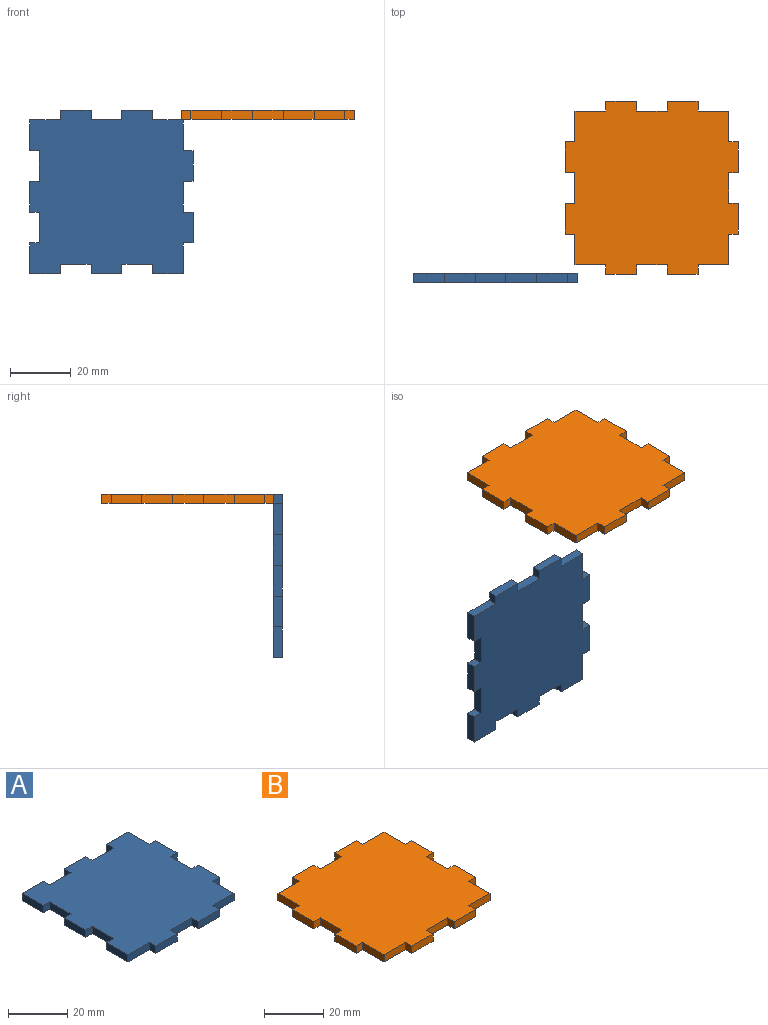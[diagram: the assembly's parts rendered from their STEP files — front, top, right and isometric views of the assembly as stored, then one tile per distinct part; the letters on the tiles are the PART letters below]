
ASSEMBLY  parts=2 mates=1
PART A: 38 faces, bbox 54x54x3 mm
  f0: plane 10.16x3mm, normal (0,1,0), area 30.5mm2, adj f1,f35,f36,f37
  f1: plane 3.18x3mm, normal (-1,0,0), area 9.5mm2, adj f0,f2,f36,f37
  f2: plane 10.16x3mm, normal (0,1,0), area 30.5mm2, adj f1,f3,f36,f37
  f3: plane 3.18x3mm, normal (1,0,0), area 9.5mm2, adj f2,f4,f36,f37
  f4: plane 10.16x3mm, normal (0,1,0), area 30.5mm2, adj f3,f5,f36,f37
  f5: plane 3.18x3mm, normal (-1,0,0), area 9.5mm2, adj f4,f6,f36,f37
  f6: plane 10.16x3mm, normal (0,1,0), area 30.5mm2, adj f5,f7,f36,f37
  f7: plane 3.18x3mm, normal (1,0,0), area 9.5mm2, adj f6,f8,f36,f37
  f8: plane 10.16x3mm, normal (0,1,0), area 30.5mm2, adj f7,f9,f36,f37
  f9: plane 10.16x3mm, normal (-1,0,0), area 30.5mm2, adj f8,f10,f36,f37
  f10: plane 3.18x3mm, normal (0,-1,0), area 9.5mm2, adj f9,f11,f36,f37
  f11: plane 10.16x3mm, normal (-1,0,0), area 30.5mm2, adj f10,f12,f36,f37
  f12: plane 3.18x3mm, normal (0,1,0), area 9.5mm2, adj f11,f13,f36,f37
  f13: plane 10.16x3mm, normal (-1,0,0), area 30.5mm2, adj f12,f14,f36,f37
  f14: plane 3.18x3mm, normal (0,-1,0), area 9.5mm2, adj f13,f15,f36,f37
  f15: plane 10.16x3mm, normal (-1,0,0), area 30.5mm2, adj f14,f16,f36,f37
  f16: plane 3.18x3mm, normal (0,1,0), area 9.5mm2, adj f15,f17,f36,f37
  f17: plane 10.16x3mm, normal (-1,0,0), area 30.5mm2, adj f16,f18,f36,f37
  f18: plane 10.16x3mm, normal (0,-1,0), area 30.5mm2, adj f17,f19,f36,f37
  f19: plane 3.18x3mm, normal (-1,0,0), area 9.5mm2, adj f18,f20,f36,f37
  f20: plane 10.16x3mm, normal (0,-1,0), area 30.5mm2, adj f19,f21,f36,f37
  f21: plane 3.18x3mm, normal (1,0,0), area 9.5mm2, adj f20,f22,f36,f37
  f22: plane 10.16x3mm, normal (0,-1,0), area 30.5mm2, adj f21,f23,f36,f37
  f23: plane 3.18x3mm, normal (-1,0,0), area 9.5mm2, adj f22,f24,f36,f37
  f24: plane 10.16x3mm, normal (0,-1,0), area 30.5mm2, adj f23,f25,f36,f37
  f25: plane 3.18x3mm, normal (1,0,0), area 9.5mm2, adj f24,f26,f36,f37
  f26: plane 10.16x3mm, normal (0,-1,0), area 30.5mm2, adj f25,f27,f36,f37
  f27: plane 10.16x3mm, normal (1,0,0), area 30.5mm2, adj f26,f28,f36,f37
  f28: plane 3.18x3mm, normal (0,-1,0), area 9.5mm2, adj f27,f29,f36,f37
  f29: plane 10.16x3mm, normal (1,0,0), area 30.5mm2, adj f28,f30,f36,f37
  f30: plane 3.18x3mm, normal (0,1,0), area 9.5mm2, adj f29,f31,f36,f37
  f31: plane 10.16x3mm, normal (1,0,0), area 30.5mm2, adj f30,f32,f36,f37
  f32: plane 3.18x3mm, normal (0,-1,0), area 9.5mm2, adj f31,f33,f36,f37
  f33: plane 10.16x3mm, normal (1,0,0), area 30.5mm2, adj f32,f34,f36,f37
  f34: plane 3.18x3mm, normal (0,1,0), area 9.5mm2, adj f33,f35,f36,f37
  f35: plane 10.16x3mm, normal (1,0,0), area 30.5mm2, adj f0,f34,f36,f37
  f36: plane 53.98x53.98mm, normal (0,0,1), area 2580.6mm2, adj f0,f1,f2,f3,f4,f5,f6,f7
  f37: plane 53.98x53.98mm, normal (0,0,-1), area 2580.6mm2, adj f0,f1,f2,f3,f4,f5,f6,f7
PART B: 38 faces, bbox 57.2x57.2x3 mm
  f0: plane 10.16x3mm, normal (-1,0,0), area 30.5mm2, adj f1,f35,f36,f37
  f1: plane 10.16x3mm, normal (0,-1,0), area 30.5mm2, adj f0,f2,f36,f37
  f2: plane 3.18x3mm, normal (-1,0,0), area 9.5mm2, adj f1,f3,f36,f37
  f3: plane 10.16x3mm, normal (0,-1,0), area 30.5mm2, adj f2,f4,f36,f37
  f4: plane 3.18x3mm, normal (1,0,0), area 9.5mm2, adj f3,f5,f36,f37
  f5: plane 10.16x3mm, normal (0,-1,0), area 30.5mm2, adj f4,f6,f36,f37
  f6: plane 3.18x3mm, normal (-1,0,0), area 9.5mm2, adj f5,f7,f36,f37
  f7: plane 10.16x3mm, normal (0,-1,0), area 30.5mm2, adj f6,f8,f36,f37
  f8: plane 3.18x3mm, normal (1,0,0), area 9.5mm2, adj f7,f9,f36,f37
  f9: plane 10.16x3mm, normal (0,-1,0), area 30.5mm2, adj f8,f10,f36,f37
  f10: plane 10.16x3mm, normal (1,0,0), area 30.5mm2, adj f9,f11,f36,f37
  f11: plane 3.18x3mm, normal (0,-1,0), area 9.5mm2, adj f10,f12,f36,f37
  f12: plane 10.16x3mm, normal (1,0,0), area 30.5mm2, adj f11,f13,f36,f37
  f13: plane 3.18x3mm, normal (0,1,0), area 9.5mm2, adj f12,f14,f36,f37
  f14: plane 10.16x3mm, normal (1,0,0), area 30.5mm2, adj f13,f15,f36,f37
  f15: plane 3.18x3mm, normal (0,-1,0), area 9.5mm2, adj f14,f16,f36,f37
  f16: plane 10.16x3mm, normal (1,0,0), area 30.5mm2, adj f15,f17,f36,f37
  f17: plane 3.18x3mm, normal (0,1,0), area 9.5mm2, adj f16,f18,f36,f37
  f18: plane 10.16x3mm, normal (1,0,0), area 30.5mm2, adj f17,f19,f36,f37
  f19: plane 10.16x3mm, normal (0,1,0), area 30.5mm2, adj f18,f20,f36,f37
  f20: plane 3.18x3mm, normal (1,0,0), area 9.5mm2, adj f19,f21,f36,f37
  f21: plane 10.16x3mm, normal (0,1,0), area 30.5mm2, adj f20,f22,f36,f37
  f22: plane 3.18x3mm, normal (-1,0,0), area 9.5mm2, adj f21,f23,f36,f37
  f23: plane 10.16x3mm, normal (0,1,0), area 30.5mm2, adj f22,f24,f36,f37
  f24: plane 3.18x3mm, normal (1,0,0), area 9.5mm2, adj f23,f25,f36,f37
  f25: plane 10.16x3mm, normal (0,1,0), area 30.5mm2, adj f24,f26,f36,f37
  f26: plane 3.18x3mm, normal (-1,0,0), area 9.5mm2, adj f25,f27,f36,f37
  f27: plane 10.16x3mm, normal (0,1,0), area 30.5mm2, adj f26,f28,f36,f37
  f28: plane 10.16x3mm, normal (-1,0,0), area 30.5mm2, adj f27,f29,f36,f37
  f29: plane 3.18x3mm, normal (0,1,0), area 9.5mm2, adj f28,f30,f36,f37
  f30: plane 10.16x3mm, normal (-1,0,0), area 30.5mm2, adj f29,f31,f36,f37
  f31: plane 3.18x3mm, normal (0,-1,0), area 9.5mm2, adj f30,f32,f36,f37
  f32: plane 10.16x3mm, normal (-1,0,0), area 30.5mm2, adj f31,f33,f36,f37
  f33: plane 3.18x3mm, normal (0,1,0), area 9.5mm2, adj f32,f34,f36,f37
  f34: plane 10.16x3mm, normal (-1,0,0), area 30.5mm2, adj f33,f35,f36,f37
  f35: plane 3.18x3mm, normal (0,-1,0), area 9.5mm2, adj f0,f34,f36,f37
  f36: plane 57.15x57.15mm, normal (0,0,1), area 2838.7mm2, adj f0,f1,f2,f3,f4,f5,f6,f7
  f37: plane 57.15x57.15mm, normal (0,0,-1), area 2838.7mm2, adj f0,f1,f2,f3,f4,f5,f6,f7
PLACE A rot(axis=(-1,0,0),90deg) t=(-31.83,-100.79,40.28)mm
PLACE B t=(-29.32,-163.85,22.43)mm
MATE planar A.f24 <-> B.f36  axis (0,0,1) through (-199.6,-99.29,25.42)mm
